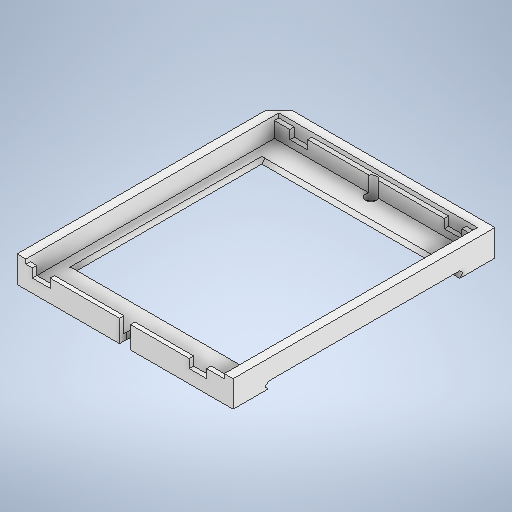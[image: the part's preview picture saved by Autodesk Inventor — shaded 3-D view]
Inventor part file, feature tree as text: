
AUTODESK INVENTOR PART (.ipt)
format: ipt  version: 2025 (Build 290162000, 162)  size: 379,392 bytes
history: native  units: in
note: dims shown in document units (in); Inventor stores cm internally (conversion verified against a paired STEP export)
features: extrude x10, sketch x9
ambient origin geometry x8: Origin, YZ Plane, XZ Plane, XY Plane, X Axis, Y Axis, Z Axis, Center Point
bodies: Solid1 (feature_tree)
feature tree (19):
  extrude  "Extrusion1"  Depth=1.9331in
  extrude  "Extrusion2"  Depth=0.0787in
  extrude  "Extrusion3"  Depth=0.0394in TaperAngle=0.0deg
  extrude  "Extrusion7"  Depth=2.2638in
  extrude  "Extrusion8"  Depth=0.0394in
  extrude  "Extrusion9"  Depth=0.0984in
  extrude  "Extrusion10"  Depth=0.0984in
  extrude  "Extrusion11"  TaperAngle=0.0deg  [1 undecoded]
  sketch  "Sketch17"  dims[d48=0.0394in d49=0.1181in d50=0.1181in d51=0.3937in d52=0.0in d53=0.1575in d54=0.1575in d55=0.0591in d56=0.1575in d57=0.1378in d58=0.0984in d59=0.1575in d60=0.1575in d61=0.0787in d62=0.0in d69=0.315in d72=45.0deg d73=45.0deg d75=45.0deg d76=45.0deg d77=0.315in d78=1.7717in d79=0.0in d80=0.1614in d81=0.0in d70=0.0344in d71=0.0197in]
  extrude  "Extrusion13"  Depth=0.1181in
  extrude  "Extrusion14"  Depth=0.1181in
  sketch  "Sketch1"  dims[d0=2.4606in d1=1.9331in]
  sketch  "Sketch2"  dims[d2=0.2362in d3=0.0in d4=0.0787in]
  sketch  "Sketch3"  dims[d5=0.0787in d6=0.0394in d7=0.0in]
  sketch  "Sketch9"  dims[d9=0.1378in d10=0.0in d36=2.2638in]
  sketch  "Sketch10"  dims[d37=0.0in d38=0.0in d39=0.0394in]
  sketch  "Sketch11"  dims[d40=0.3937in d41=0.0in d42=0.0984in]
  sketch  "Sketch12"  dims[d43=0.0984in d44=2.1378in]
  sketch  "Sketch13"  dims[d45=1.0886in d46=0.0in d47=0.0in]
note: 1 required parameter value undecoded (feature->parameter linkage not recoverable at this tier; creation-order binding heuristic only, values carry confidence <= 0.55)
